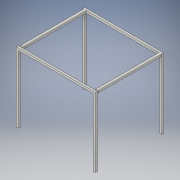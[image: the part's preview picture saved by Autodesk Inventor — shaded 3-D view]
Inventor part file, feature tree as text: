
AUTODESK INVENTOR PART (.ipt)
format: ipt  version: 2019 (Build 230136000, 136)  size: 133,632 bytes
history: native  units: in
note: dims shown in document units (in); Inventor stores cm internally (conversion verified against a paired STEP export)
features: sketch x4, sweep x2, plane x2, mirror x2
ambient origin geometry x8: Origin, YZ Plane, XZ Plane, XY Plane, X Axis, Y Axis, Z Axis, Center Point
bodies: Body1 (feature_tree)
feature tree (10):
  sweep  "Sweep3"
  plane  "Work Plane1"
  mirror  "Mirror1"
  sweep  "Sweep4"
  plane  "Work Plane2"
  mirror  "Mirror2"
  sketch  "3D Sketch1"
  sketch  "Sketch3"  dims[d0=16.0in d1=18.0in]
  sketch  "3D Sketch2"
  sketch  "Sketch4"  dims[d2=18.0in d3=16.0in d4=16.0in d5=16.0in d6=16.0in d7=0.5in d12=0.0in d13=0.0in d14=-8.0in d15=0.0in d16=0.0in d17=8.5in]
